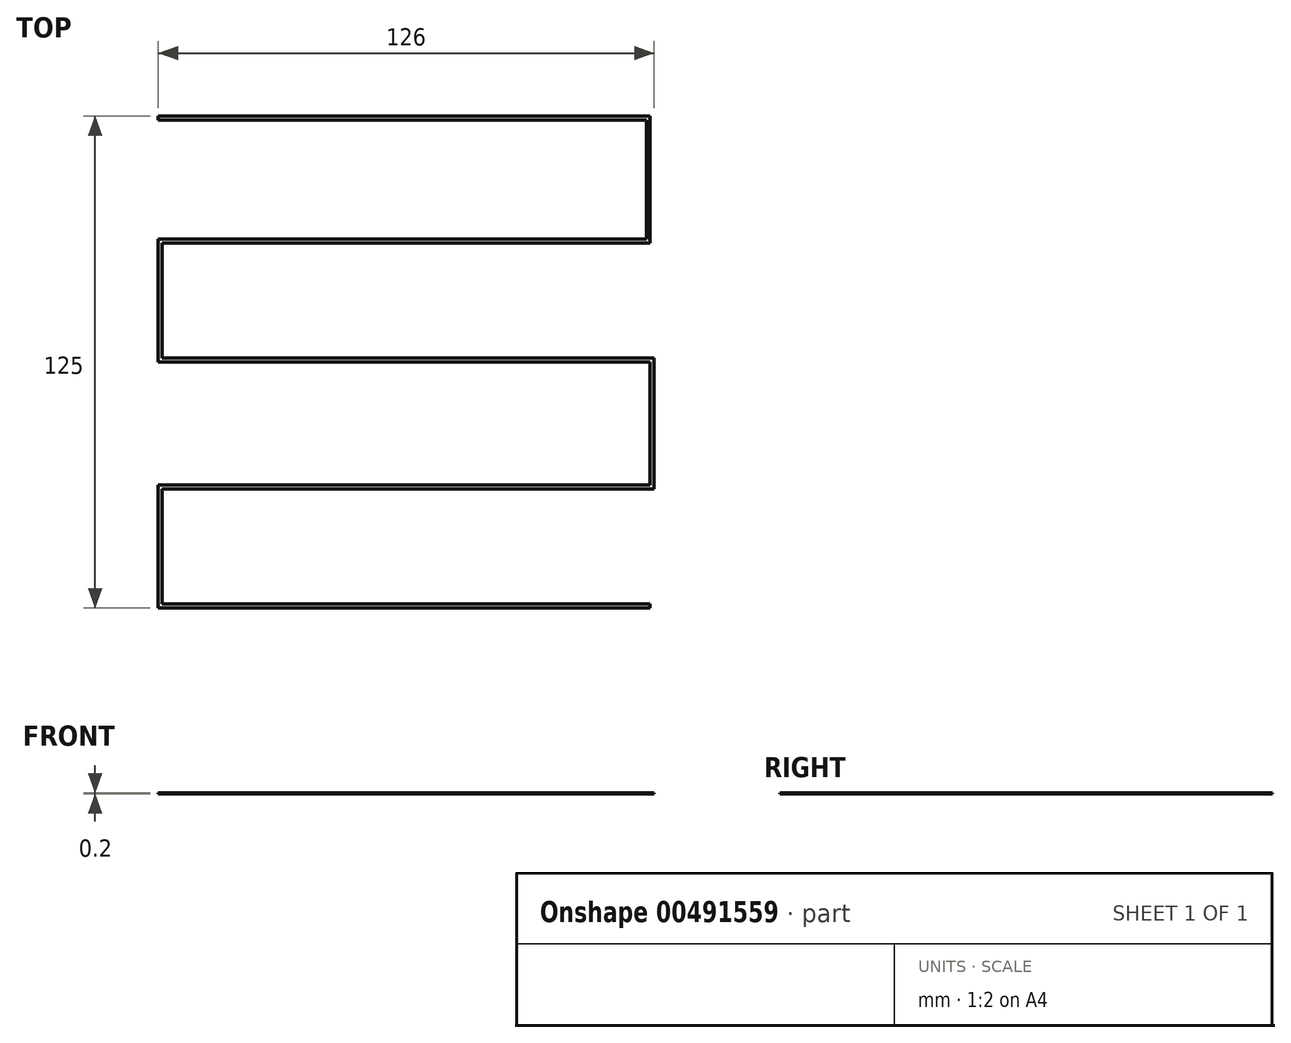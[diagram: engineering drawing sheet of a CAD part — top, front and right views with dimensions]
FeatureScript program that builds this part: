
annotation { "Feature Type Name" : "Feature", "Feature Type Description" : "" }
export const myFeature = defineFeature(function(context is Context, id is Id, definition is map)
    precondition{}
    {
        {
            var Q0;
            Q0=qCreatedBy(makeId("Top.planeOp"),FACE);
            var sketch = newSketch(context, id + "F0", { "sketchPlane" : qUnion([Q0])});
            skLineSegment(sketch, "E0.left", {"start": v(-62.5, 31.25) * mm, "end": v(-62.5, 0) * mm});
            skPoint(sketch, "E0.middle", {"position": v(0, 0) * mm});
            skLineSegment(sketch, "E1", {"start": v(-62.5, 0) * mm, "end": v(62.5, 0) * mm});
            skPoint(sketch, "E2.orphan", {"position": v(62.5, -62.5) * mm});
            skLineSegment(sketch, "E3", {"start": v(62.5, -31.25) * mm, "end": v(62.5, 0) * mm});
            skLineSegment(sketch, "E4", {"start": v(-62.5, -31.25) * mm, "end": v(-62.5, -62.5) * mm});
            skLineSegment(sketch, "E5", {"start": v(-62.5, 31.25) * mm, "end": v(61.5, 31.25) * mm});
            skLineSegment(sketch, "E6", {"start": v(-62.5, -31.25) * mm, "end": v(62.5, -31.25) * mm});
            skPoint(sketch, "E7.orphan", {"position": v(-31.25, 62.5) * mm});
            skPoint(sketch, "E8.orphan", {"position": v(31.25, 62.5) * mm});
            skPoint(sketch, "E9.end.orphan", {"position": v(-31.25, -62.5) * mm});
            skPoint(sketch, "E10.end.orphan", {"position": v(31.25, -62.5) * mm});
            skLineSegment(sketch, "E11", {"start": v(-62.5, 62.5) * mm, "end": v(62.5, 62.5) * mm});
            skLineSegment(sketch, "E12", {"start": v(-62.5, -62.5) * mm, "end": v(62.5, -62.5) * mm});
            skLineSegment(sketch, "E13.0", {"start": v(-62.5, 61.5) * mm, "end": v(61.5, 61.5) * mm});
            skLineSegment(sketch, "E14.0", {"start": v(61.5, 61.5) * mm, "end": v(61.5, 31.25) * mm});
            skLineSegment(sketch, "E15.0", {"start": v(-61.5, 30.25) * mm, "end": v(62.5, 30.25) * mm});
            skLineSegment(sketch, "E15.1", {"start": v(-61.5, 30.25) * mm, "end": v(-61.5, 1) * mm});
            skLineSegment(sketch, "E15.2", {"start": v(-61.5, 1) * mm, "end": v(63.5, 1) * mm});
            skLineSegment(sketch, "E15.3", {"start": v(-61.5, -61.5) * mm, "end": v(62.5, -61.5) * mm});
            skLineSegment(sketch, "E15.4", {"start": v(-61.5, -32.25) * mm, "end": v(-61.5, -61.5) * mm});
            skLineSegment(sketch, "E15.5", {"start": v(-61.5, -32.25) * mm, "end": v(63.5, -32.25) * mm});
            skLineSegment(sketch, "E15.6", {"start": v(63.5, -32.25) * mm, "end": v(63.5, 1) * mm});
            skLineSegment(sketch, "E16", {"start": v(-62.5, 62.5) * mm, "end": v(-62.5, 61.5) * mm});
            skPoint(sketch, "E0.right.end.orphan", {"position": v(62.5, 31.25) * mm});
            skLineSegment(sketch, "E17", {"start": v(62.5, 30.25) * mm, "end": v(62.5, 62.5) * mm});
            skLineSegment(sketch, "E18", {"start": v(62.5, -61.5) * mm, "end": v(62.5, -62.5) * mm});
            skSolve(sketch);
        }
        {
            var Q0;
            Q0=makeQuery(id+"F0.imprint","IMPRINT",FACE,{"disambiguationData":[TD([[makeQuery(id+"F0.imprint","IMPRINT",EDGE,{"derivedFrom":sQuery(id+"F0.wireOp",EDGE,"E0.left")}),1.0]])]});
            extrude(context, id + "F1", {"entities" : qUnion([Q0]), "depth" : 0.2 * mm, "offsetDistance" : 25 * mm});
        }
    });
